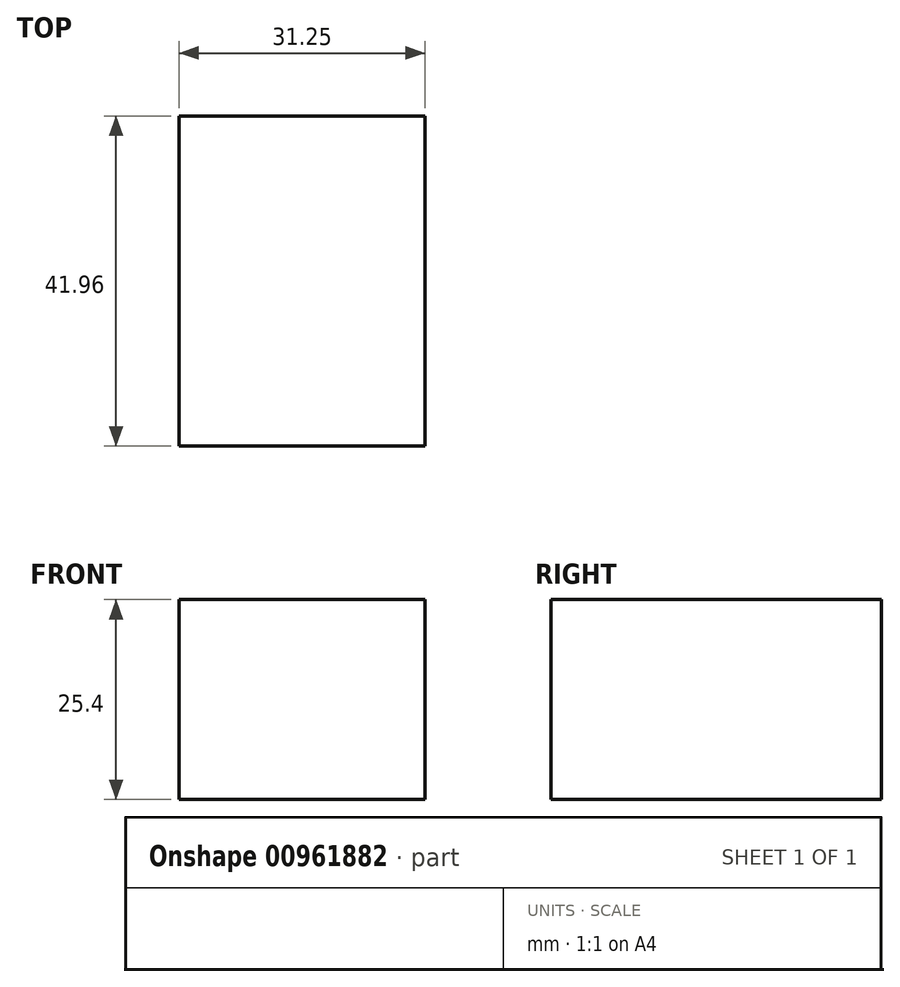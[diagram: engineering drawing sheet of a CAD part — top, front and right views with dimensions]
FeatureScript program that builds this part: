
annotation { "Feature Type Name" : "Feature", "Feature Type Description" : "" }
export const myFeature = defineFeature(function(context is Context, id is Id, definition is map)
    precondition{}
    {
        {
            var Q0;
            Q0=qCreatedBy(makeId("Top.planeOp"),FACE);
            var sketch = newSketch(context, id + "F0", { "sketchPlane" : qUnion([Q0])});
            skLineSegment(sketch, "E0.bottom", {"start": v(-14.9, 19.97) * mm, "end": v(16.35, 19.97) * mm});
            skLineSegment(sketch, "E0.top", {"start": v(-14.9, -22) * mm, "end": v(16.35, -22) * mm});
            skLineSegment(sketch, "E0.left", {"start": v(-14.9, 19.97) * mm, "end": v(-14.9, -22) * mm});
            skLineSegment(sketch, "E0.right", {"start": v(16.35, 19.97) * mm, "end": v(16.35, -22) * mm});
            skSolve(sketch);
        }
        {
            var Q0;
            Q0 = qSketchRegion(id + "F0", true);
            extrude(context, id + "F1", {"entities" : qUnion([Q0]), "depth" : 25.4 * mm, "offsetDistance" : 25.4 * mm});
        }
    });
